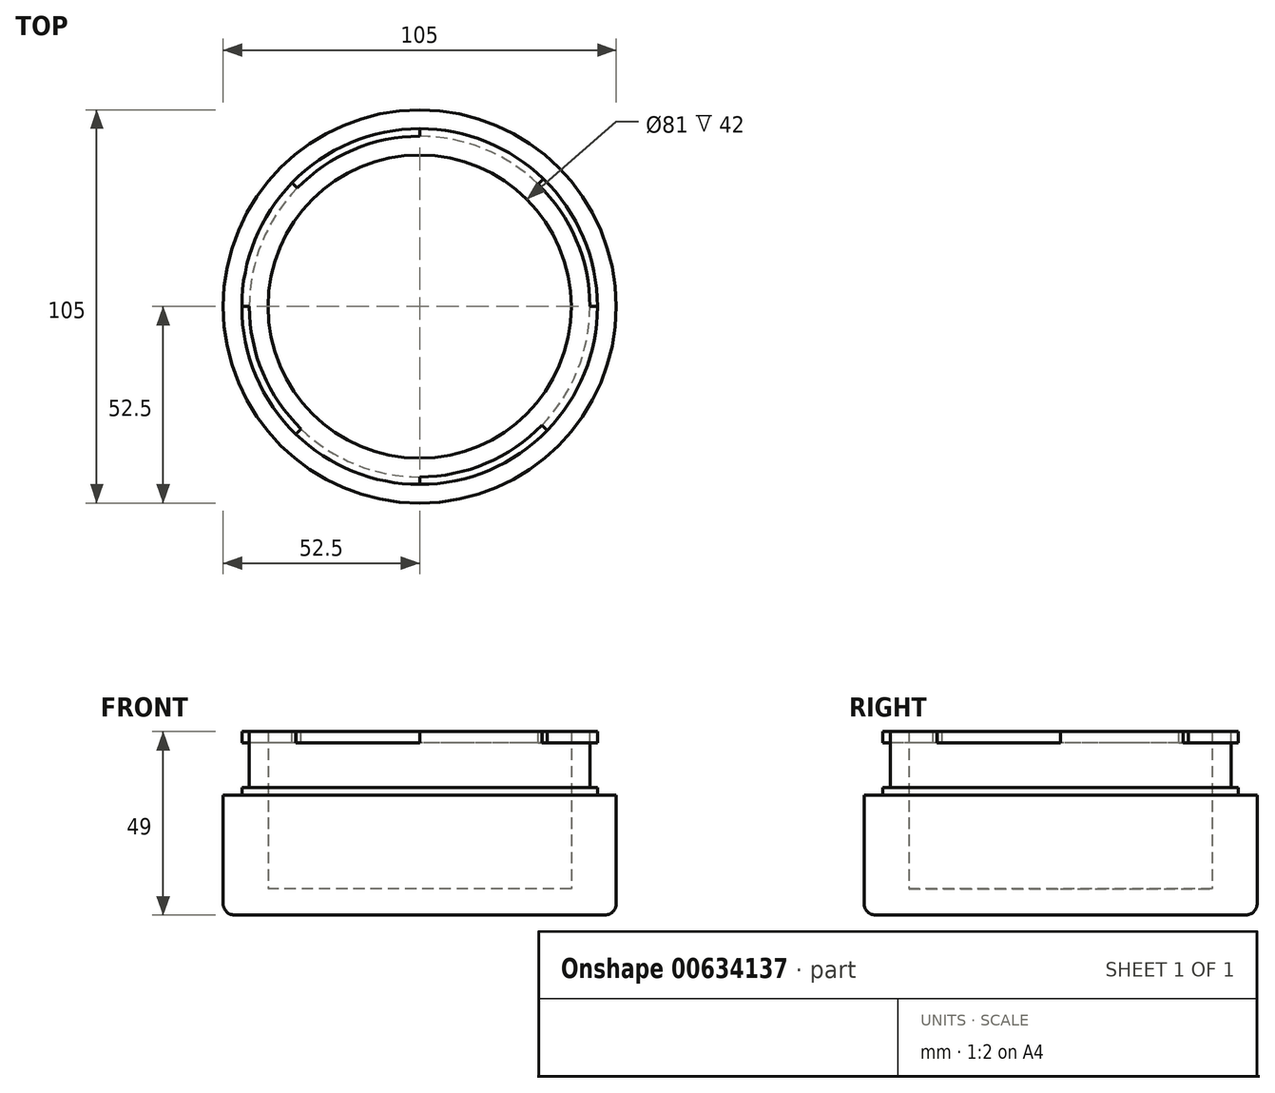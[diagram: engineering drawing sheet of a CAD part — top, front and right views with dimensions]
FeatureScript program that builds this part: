
annotation { "Feature Type Name" : "Feature", "Feature Type Description" : "" }
export const myFeature = defineFeature(function(context is Context, id is Id, definition is map)
    precondition{}
    {
        {
            var Q0;
            Q0=qCreatedBy(makeId("Top.planeOp"),FACE);
            var sketch = newSketch(context, id + "F0", { "sketchPlane" : qUnion([Q0])});
            skCircle(sketch, "E0", {"center": v(0, 0) * mm, "radius": 52.5 * mm});
            skSolve(sketch);
        }
        {
            var Q0;
            Q0=makeQuery(id+"F0.imprint","IMPRINT",FACE,{"disambiguationData":[TD([[makeQuery(id+"F0.imprint","IMPRINT",EDGE,{"derivedFrom":sQuery(id+"F0.wireOp",EDGE,"E0")}),1.0]])]});
            extrude(context, id + "F1", {"entities" : qUnion([Q0]), "depth" : 32 * mm, "offsetDistance" : 25 * mm});
        }
        {
            var Q0;
            Q0=makeQuery(id+"F1.opExtrude","CAP_FACE",FACE,{"disambiguationData":[OSD([sQuery(id+"F0.wireOp",EDGE,"E0")])],"isStart":false});
            shell(context, id + "F2", {"entities" : qUnion([Q0]), "thickness" : 7 * mm});
        }
        {
            var Q0;
            {var subQ0=sQuery(id+"F0.wireOp",EDGE,"E0");Q0=makeQuery(id+"F2.opShell","OFFSET_FACE",FACE,{"disambiguationData":[OSD([subQ0]),TDD([makeQuery(id+"F1.opExtrude","CAP_FACE",FACE,{"disambiguationData":[OSD([subQ0])],"isStart":true})])]});}
            var sketch = newSketch(context, id + "F3", { "sketchPlane" : qUnion([Q0])});
            skCircle(sketch, "E1", {"center": v(0, 0) * mm, "radius": 40.5 * mm});
            skSolve(sketch);
        }
        {
            var Q0;
            Q0=makeQuery(id+"F3.imprint","IMPRINT",FACE,{"disambiguationData":[TD([[makeQuery(id+"F3.imprint","IMPRINT",EDGE,{"derivedFrom":sQuery(id+"F3.wireOp",EDGE,"E1")}),-1.0]])]});
            extrude(context, id + "F4", {"entities" : qUnion([Q0]), "operationType" : NewBodyOperationType.ADD, "depth" : 42 * mm, "offsetDistance" : 25 * mm});
        }
        {
            var Q0;
            Q0=makeQuery(id+"F1.opExtrude","CAP_EDGE",EDGE,{"disambiguationData":[OSD([sQuery(id+"F0.wireOp",EDGE,"E0")])],"isStart":true});
            fillet(context, id + "F5", {"entities" : qUnion([Q0]), "radius" : 3 * mm, "tangentPropagation" : true, "allowEdgeOverflow" : false});
        }
        {
            var Q0;
            Q0=makeQuery(id+"F1.opExtrude","CAP_FACE",FACE,{"disambiguationData":[OSD([sQuery(id+"F0.wireOp",EDGE,"E0")])],"isStart":false});
            var sketch = newSketch(context, id + "F6", { "sketchPlane" : qUnion([Q0])});
            skCircle(sketch, "E2", {"center": v(0, 0) * mm, "radius": 47.5 * mm});
            skSolve(sketch);
        }
        {
            var Q0;
            Q0=makeQuery(id+"F6.imprint","IMPRINT",FACE,{"disambiguationData":[TD([[makeQuery(id+"F6.imprint","IMPRINT",EDGE,{"derivedFrom":sQuery(id+"F6.wireOp",EDGE,"E2")}),1.0]])]});
            extrude(context, id + "F7", {"entities" : qUnion([Q0]), "operationType" : NewBodyOperationType.ADD, "depth" : 2 * mm, "offsetDistance" : 25 * mm});
        }
        {
            var Q0;
            Q0=makeQuery(id+"F4.opExtrude","CAP_FACE",FACE,{"disambiguationData":[OSD([sQuery(id+"F0.wireOp",EDGE,"E0"),sQuery(id+"F3.wireOp",EDGE,"E1")])],"isStart":false});
            var sketch = newSketch(context, id + "F8", { "sketchPlane" : qUnion([Q0])});
            skArc(sketch, "E3", {"start": v(0, 45.5) * mm, "mid": v(17.07, 42.18) * mm, "end": v(31.65, 32.69) * mm});
            skArc(sketch, "E4", {"start": v(45.5, 0) * mm, "mid": v(42.18, -17.07) * mm, "end": v(32.69, -31.65) * mm});
            skArc(sketch, "E5", {"start": v(0, -45.5) * mm, "mid": v(-17.07, -42.18) * mm, "end": v(-31.65, -32.69) * mm});
            skArc(sketch, "E6", {"start": v(-45.5, 0) * mm, "mid": v(-42.18, 17.07) * mm, "end": v(-32.69, 31.65) * mm});
            skArc(sketch, "E7", {"start": v(0, 47.5) * mm, "mid": v(17.82, 44.03) * mm, "end": v(33.04, 34.13) * mm});
            skArc(sketch, "E8", {"start": v(47.5, 0) * mm, "mid": v(44.03, -17.82) * mm, "end": v(34.13, -33.04) * mm});
            skArc(sketch, "E9", {"start": v(0, -47.5) * mm, "mid": v(-17.82, -44.03) * mm, "end": v(-33.04, -34.13) * mm});
            skArc(sketch, "E10", {"start": v(-47.5, 0) * mm, "mid": v(-44.03, 17.82) * mm, "end": v(-34.13, 33.04) * mm});
            skLineSegment(sketch, "E11", {"start": v(0, 45.5) * mm, "end": v(0, 47.5) * mm});
            skLineSegment(sketch, "E12", {"start": v(31.65, 32.69) * mm, "end": v(33.04, 34.13) * mm});
            skLineSegment(sketch, "E13", {"start": v(45.5, 0) * mm, "end": v(47.5, 0) * mm});
            skLineSegment(sketch, "E14", {"start": v(32.69, -31.65) * mm, "end": v(34.13, -33.04) * mm});
            skLineSegment(sketch, "E15", {"start": v(0, -45.5) * mm, "end": v(0, -47.5) * mm});
            skLineSegment(sketch, "E16", {"start": v(-31.65, -32.69) * mm, "end": v(-33.04, -34.13) * mm});
            skLineSegment(sketch, "E17", {"start": v(-47.5, 0) * mm, "end": v(-45.5, 0) * mm});
            skLineSegment(sketch, "E18", {"start": v(-32.69, 31.65) * mm, "end": v(-34.13, 33.04) * mm});
            skSolve(sketch);
        }
        {
            var Q0;
            Q0=makeQuery(id+"F8.imprint","IMPRINT",FACE,{"disambiguationData":[TD([[makeQuery(id+"F8.imprint","IMPRINT",EDGE,{"derivedFrom":sQuery(id+"F8.wireOp",EDGE,"E3")}),-1.0]])]});
            var Q1;
            Q1=makeQuery(id+"F8.imprint","IMPRINT",FACE,{"disambiguationData":[TD([[makeQuery(id+"F8.imprint","IMPRINT",EDGE,{"derivedFrom":sQuery(id+"F8.wireOp",EDGE,"E4")}),-1.0]])]});
            var Q2;
            Q2=makeQuery(id+"F8.imprint","IMPRINT",FACE,{"disambiguationData":[TD([[makeQuery(id+"F8.imprint","IMPRINT",EDGE,{"derivedFrom":sQuery(id+"F8.wireOp",EDGE,"E5")}),-1.0]])]});
            var Q3;
            Q3=makeQuery(id+"F8.imprint","IMPRINT",FACE,{"disambiguationData":[TD([[makeQuery(id+"F8.imprint","IMPRINT",EDGE,{"derivedFrom":sQuery(id+"F8.wireOp",EDGE,"E6")}),-1.0]])]});
            extrude(context, id + "F9", {"entities" : qUnion([Q0, Q1, Q2, Q3]), "operationType" : NewBodyOperationType.ADD, "depth" : -3 * mm, "offsetDistance" : 25 * mm});
        }
    });
